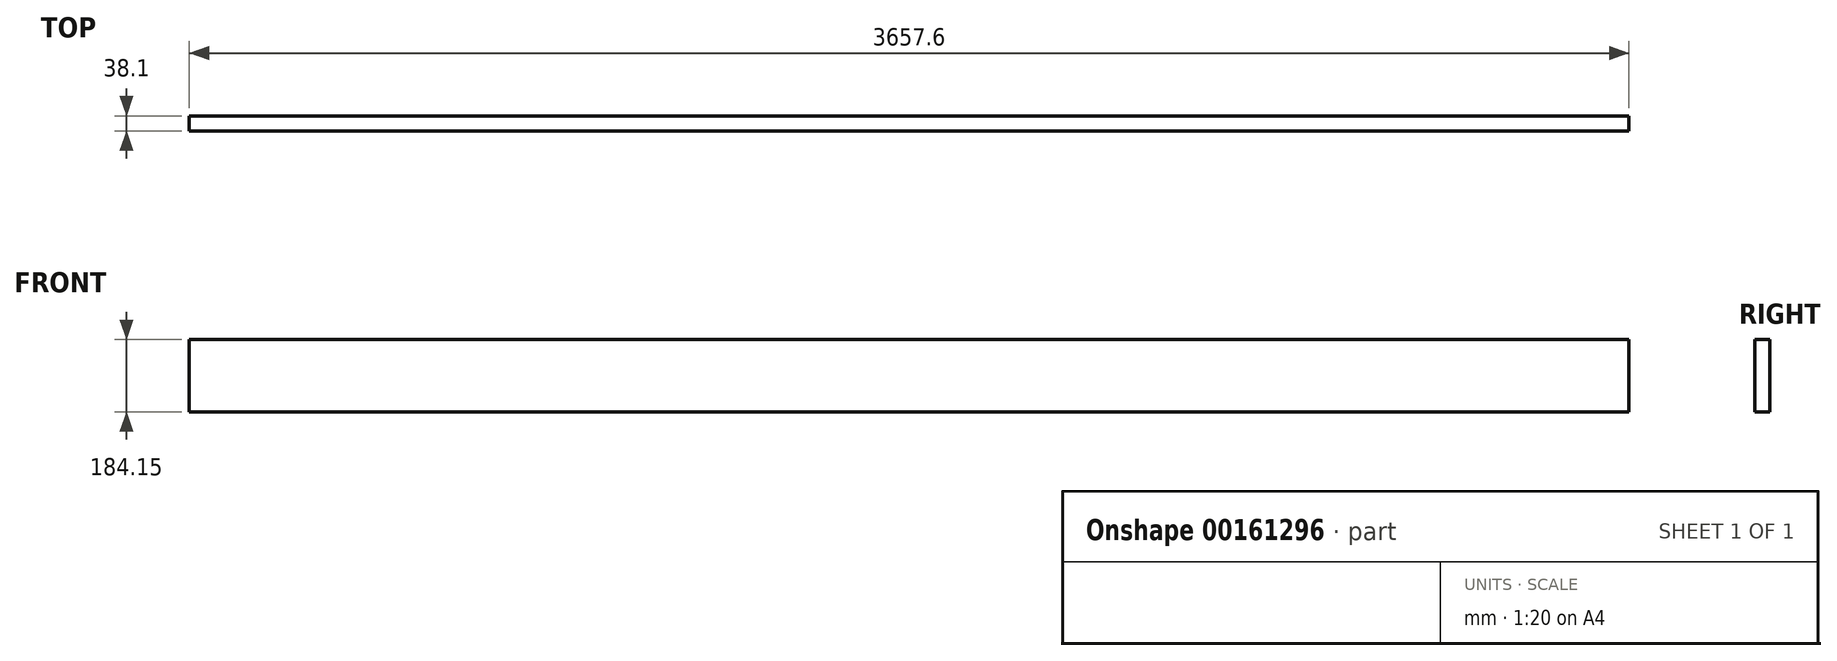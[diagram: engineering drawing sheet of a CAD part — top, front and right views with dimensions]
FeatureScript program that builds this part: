
annotation { "Feature Type Name" : "Feature", "Feature Type Description" : "" }
export const myFeature = defineFeature(function(context is Context, id is Id, definition is map)
    precondition{}
    {
        {
            var Q0;
            Q0=qCreatedBy(makeId("Front.planeOp"),FACE);
            var sketch = newSketch(context, id + "F0", { "sketchPlane" : qUnion([Q0])});
            skLineSegment(sketch, "E0.bottom", {"start": v(-1828.8, 184.15) * mm, "end": v(1828.8, 184.15) * mm});
            skLineSegment(sketch, "E0.top", {"start": v(-1828.8, 0) * mm, "end": v(1828.8, 0) * mm});
            skLineSegment(sketch, "E0.left", {"start": v(-1828.8, 184.15) * mm, "end": v(-1828.8, 0) * mm});
            skLineSegment(sketch, "E0.right", {"start": v(1828.8, 184.15) * mm, "end": v(1828.8, 0) * mm});
            skSolve(sketch);
        }
        {
            var Q0;
            Q0 = qSketchRegion(id + "F0", true);
            extrude(context, id + "F1", {"entities" : qUnion([Q0]), "depth" : 38.1 * mm});
        }
    });
